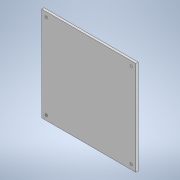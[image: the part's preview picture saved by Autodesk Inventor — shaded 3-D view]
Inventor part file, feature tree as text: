
AUTODESK INVENTOR PART (.ipt)
format: ipt  version: 2022 (Build 260153000, 153)  size: 106,496 bytes
history: native  units: in
note: dims shown in document units (in); Inventor stores cm internally (conversion verified against a paired STEP export)
features: extrude x1, sketch x1
ambient origin geometry x8: Origin, YZ Plane, XZ Plane, XY Plane, X Axis, Y Axis, Z Axis, Center Point
bodies: Solid1 (feature_tree)
feature tree (2):
  extrude  "Extrusion1"  Depth=5.0in
  sketch  "Sketch1"  dims[d0=5.0in d1=5.0in d2=5.0in d3=0.12in d4=0.12in d5=0.25in d6=0.25in d7=0.25in d8=0.25in d9=0.125in d10=0.0in]
